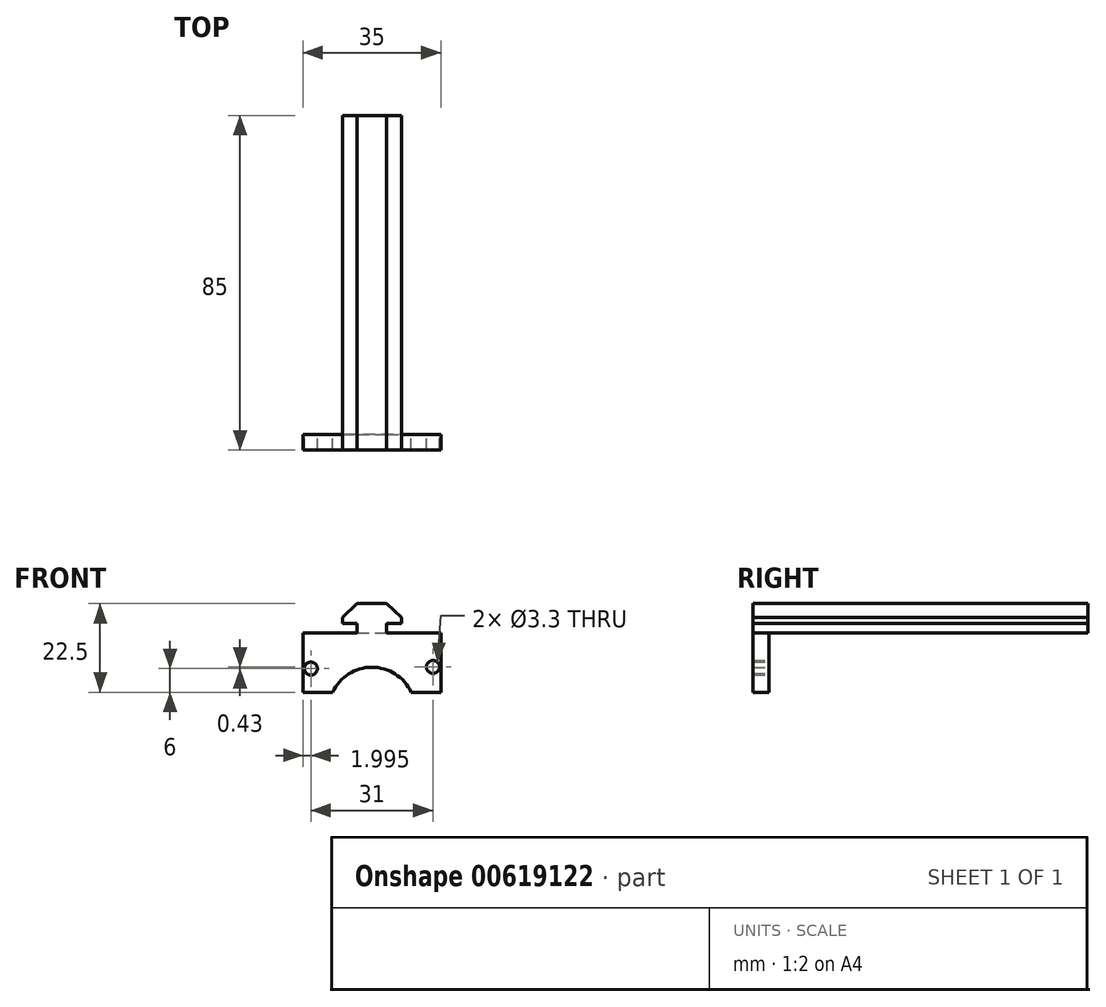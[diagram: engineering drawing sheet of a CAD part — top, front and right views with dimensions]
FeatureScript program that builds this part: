
annotation { "Feature Type Name" : "Feature", "Feature Type Description" : "" }
export const myFeature = defineFeature(function(context is Context, id is Id, definition is map)
    precondition{}
    {
        {
            var Q0;
            Q0=qCreatedBy(makeId("Front.planeOp"),FACE);
            var sketch = newSketch(context, id + "F0", { "sketchPlane" : qUnion([Q0])});
            skLineSegment(sketch, "E0", {"start": v(-3.77, 0) * mm, "end": v(-3.77, 2.5) * mm});
            skLineSegment(sketch, "E1", {"start": v(-3.77, 2.5) * mm, "end": v(-7.52, 2.5) * mm});
            skLineSegment(sketch, "E2", {"start": v(-7.52, 2.5) * mm, "end": v(-7.52, 4) * mm});
            skLineSegment(sketch, "E3", {"start": v(-7.52, 4) * mm, "end": v(-3.77, 7.5) * mm});
            skLineSegment(sketch, "E4", {"start": v(-3.77, 7.5) * mm, "end": v(3.73, 7.5) * mm});
            skLineSegment(sketch, "E5", {"start": v(3.73, 7.5) * mm, "end": v(7.48, 4) * mm});
            skLineSegment(sketch, "E6", {"start": v(7.48, 4) * mm, "end": v(7.48, 2.5) * mm});
            skLineSegment(sketch, "E7", {"start": v(7.48, 2.5) * mm, "end": v(3.73, 2.5) * mm});
            skLineSegment(sketch, "E8", {"start": v(3.73, 2.5) * mm, "end": v(3.73, 0) * mm});
            skLineSegment(sketch, "E9", {"start": v(3.73, 0) * mm, "end": v(-3.77, 0) * mm});
            skSolve(sketch);
        }
        {
            var Q0;
            Q0=qSketchRegion(id+"F0",true);
            extrude(context, id + "F1", {"entities" : qUnion([Q0]), "depth" : 85 * mm, "offsetDistance" : 25 * mm});
        }
        {
            var Q0;
            Q0=makeQuery(id+"F1.opExtrude","CAP_FACE",FACE,{"disambiguationData":[OSD([sQuery(id+"F0.wireOp",EDGE,"E0"),sQuery(id+"F0.wireOp",EDGE,"E1"),sQuery(id+"F0.wireOp",EDGE,"E2"),sQuery(id+"F0.wireOp",EDGE,"E3"),sQuery(id+"F0.wireOp",EDGE,"E4"),sQuery(id+"F0.wireOp",EDGE,"E5"),sQuery(id+"F0.wireOp",EDGE,"E6"),sQuery(id+"F0.wireOp",EDGE,"E7"),sQuery(id+"F0.wireOp",EDGE,"E8"),sQuery(id+"F0.wireOp",EDGE,"E9")])],"isStart":false});
            var sketch = newSketch(context, id + "F2", { "sketchPlane" : qUnion([Q0])});
            skLineSegment(sketch, "E10.bottom", {"start": v(-17.52, 0) * mm, "end": v(17.48, 0) * mm});
            skLineSegment(sketch, "E10.top", {"start": v(-17.52, -15) * mm, "end": v(17.48, -15) * mm});
            skLineSegment(sketch, "E10.left", {"start": v(-17.52, 0) * mm, "end": v(-17.52, -15) * mm});
            skLineSegment(sketch, "E10.right", {"start": v(17.48, 0) * mm, "end": v(17.48, -15) * mm});
            skSolve(sketch);
        }
        {
            var Q0;
            Q0 = qSketchRegion(id + "F2", true);
            extrude(context, id + "F3", {"entities" : qUnion([Q0]), "operationType" : NewBodyOperationType.ADD, "oppositeDirection" : true, "depth" : 4 * mm, "offsetDistance" : 25 * mm});
        }
        {
            var Q0;
            Q0=makeQuery(id+"F3.boolean.opBoolean","MERGE",FACE,{"derivedFrom":[makeQuery(id+"F1.opExtrude","CAP_FACE",FACE,{"disambiguationData":[OSD([sQuery(id+"F0.wireOp",EDGE,"E0"),sQuery(id+"F0.wireOp",EDGE,"E1"),sQuery(id+"F0.wireOp",EDGE,"E2"),sQuery(id+"F0.wireOp",EDGE,"E3"),sQuery(id+"F0.wireOp",EDGE,"E4"),sQuery(id+"F0.wireOp",EDGE,"E5"),sQuery(id+"F0.wireOp",EDGE,"E6"),sQuery(id+"F0.wireOp",EDGE,"E7"),sQuery(id+"F0.wireOp",EDGE,"E8"),sQuery(id+"F0.wireOp",EDGE,"E9")])],"isStart":false}),makeQuery(id+"F3.opExtrude","CAP_FACE",FACE,{"disambiguationData":[OSD([sQuery(id+"F2.wireOp",EDGE,"E10.bottom"),sQuery(id+"F2.wireOp",EDGE,"E10.top"),sQuery(id+"F2.wireOp",EDGE,"E10.left"),sQuery(id+"F2.wireOp",EDGE,"E10.right")])],"isStart":true})]});
            var sketch = newSketch(context, id + "F4", { "sketchPlane" : qUnion([Q0])});
            skPoint(sketch, "E11", {"position": v(-15.52, -9) * mm});
            skPoint(sketch, "E12", {"position": v(15.48, -8.57) * mm});
            skSolve(sketch);
        }
        {
            var Q0;
            Q0=sQuery(id+"F4.wireOp",VERTEX,"E11");
            var Q1;
            Q1=sQuery(id+"F4.wireOp",VERTEX,"E12");
            var Q2;
            Q2=makeQuery(id+"F1.opExtrude","SWEPT_BODY",BODY,{"disambiguationData":[OSD([sQuery(id+"F0.wireOp",EDGE,"E0"),sQuery(id+"F0.wireOp",EDGE,"E1"),sQuery(id+"F0.wireOp",EDGE,"E2"),sQuery(id+"F0.wireOp",EDGE,"E3"),sQuery(id+"F0.wireOp",EDGE,"E4"),sQuery(id+"F0.wireOp",EDGE,"E5"),sQuery(id+"F0.wireOp",EDGE,"E6"),sQuery(id+"F0.wireOp",EDGE,"E7"),sQuery(id+"F0.wireOp",EDGE,"E8"),sQuery(id+"F0.wireOp",EDGE,"E9")])]});
            hole(context, id + "F5", {"style" : HoleStyle.SIMPLE, "endStyle" : HoleEndStyle.BLIND, "standardTappedOrClearance" : lookupTablePath({ "standard" : "ISO", "fit" : "Normal", "size" : "M3", "type" : "Clearance" }), "standardBlindInLast" : lookupTablePath({ "fit" : "Standard", "standard" : "ISO", "size" : "M3", "type" : "Clearance" }), "holeDiameter" : 3.3 * mm, "majorDiameter" : 5 * mm, "holeDepth" : 30 * mm, "isTappedThrough" : true, "tappedDepth" : 12 * mm, "tapClearance" : 3, "locations" : qUnion([Q0, Q1]), "scope" : qUnion([Q2]), "startStyle" : HoleStartStyle.SKETCH});
        }
        {
            var Q0;
            Q0=makeQuery(id+"F3.boolean.opBoolean","MERGE",FACE,{"derivedFrom":[makeQuery(id+"F1.opExtrude","CAP_FACE",FACE,{"disambiguationData":[OSD([sQuery(id+"F0.wireOp",EDGE,"E0"),sQuery(id+"F0.wireOp",EDGE,"E1"),sQuery(id+"F0.wireOp",EDGE,"E2"),sQuery(id+"F0.wireOp",EDGE,"E3"),sQuery(id+"F0.wireOp",EDGE,"E4"),sQuery(id+"F0.wireOp",EDGE,"E5"),sQuery(id+"F0.wireOp",EDGE,"E6"),sQuery(id+"F0.wireOp",EDGE,"E7"),sQuery(id+"F0.wireOp",EDGE,"E8"),sQuery(id+"F0.wireOp",EDGE,"E9")])],"isStart":false}),makeQuery(id+"F3.opExtrude","CAP_FACE",FACE,{"disambiguationData":[OSD([sQuery(id+"F2.wireOp",EDGE,"E10.bottom"),sQuery(id+"F2.wireOp",EDGE,"E10.top"),sQuery(id+"F2.wireOp",EDGE,"E10.left"),sQuery(id+"F2.wireOp",EDGE,"E10.right")])],"isStart":true})]});
            var sketch = newSketch(context, id + "F6", { "sketchPlane" : qUnion([Q0])});
            skPoint(sketch, "E13", {"position": v(0, -19.64) * mm});
            skSolve(sketch);
        }
        {
            var Q0;
            Q0=sQuery(id+"F6.wireOp",VERTEX,"E13");
            var Q1;
            Q1=makeQuery(id+"F1.opExtrude","SWEPT_BODY",BODY,{"disambiguationData":[OSD([sQuery(id+"F0.wireOp",EDGE,"E0"),sQuery(id+"F0.wireOp",EDGE,"E1"),sQuery(id+"F0.wireOp",EDGE,"E2"),sQuery(id+"F0.wireOp",EDGE,"E3"),sQuery(id+"F0.wireOp",EDGE,"E4"),sQuery(id+"F0.wireOp",EDGE,"E5"),sQuery(id+"F0.wireOp",EDGE,"E6"),sQuery(id+"F0.wireOp",EDGE,"E7"),sQuery(id+"F0.wireOp",EDGE,"E8"),sQuery(id+"F0.wireOp",EDGE,"E9")])]});
            hole(context, id + "F7", {"style" : HoleStyle.SIMPLE, "endStyle" : HoleEndStyle.BLIND, "standardTappedOrClearance" : lookupTablePath({ "standard" : "ISO", "fit" : "Normal", "size" : "M20", "type" : "Clearance" }), "standardBlindInLast" : lookupTablePath({ "fit" : "Standard", "standard" : "ISO", "size" : "M20", "type" : "Clearance" }), "holeDiameter" : 22 * mm, "majorDiameter" : 5 * mm, "holeDepth" : 30 * mm, "isTappedThrough" : true, "tappedDepth" : 12 * mm, "tapClearance" : 3, "locations" : qUnion([Q0]), "scope" : qUnion([Q1]), "startStyle" : HoleStartStyle.SKETCH});
        }
    });
